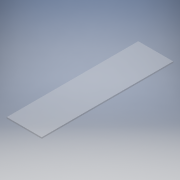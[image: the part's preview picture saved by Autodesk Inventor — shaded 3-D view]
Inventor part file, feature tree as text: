
AUTODESK INVENTOR PART (.ipt)
format: ipt  version: 2018 (Build 220112000, 112)  size: 109,056 bytes
history: native  units: mm
features: extrude x1, sketch x1
ambient origin geometry x8: Origin, YZ Plane, XZ Plane, XY Plane, X Axis, Y Axis, Z Axis, Center Point
bodies: Volumenkörper1 (feature_tree)
feature tree (2):
  extrude  "Extrusion1"  Depth=155.0mm
  sketch  "Skizze1"  dims[d0=583.0mm d1=155.0mm d2=6.0mm d3=0.0mm]
